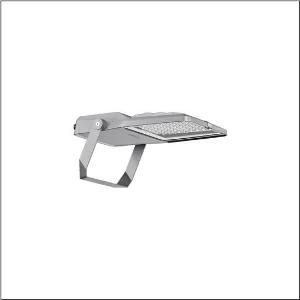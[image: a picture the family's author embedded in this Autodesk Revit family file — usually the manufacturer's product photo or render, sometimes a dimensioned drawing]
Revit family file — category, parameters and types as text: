
# Revit family: floodlight_fl_21_iq_mini___pl64_5xa7772d1e1a_af72
name_source: partatom
category: Lighting Fixtures
units: mm (PartAtom-declared; Revit-internal decimal feet)

## family parameters
Cut with Voids When Loaded = No
Host = Face
Light Source = No
Part Type = Normal
Room Calculation Point = No
Round Connector Dimension = Use Diameter
Shared = No

## types (1)
- --- (1 x LED, 14250 lm, 143 W, 2200K)
    Apparent Load = 143 VA
    CIE Flux Codes = 28 80 98 100 100
    Color Rendering = 70
    Color Temperature = 2200K
    Default Elevation = 1800 mm
    Description = Floodlight FL 21 iQ mini, floodlight, primary light control with lens, of PMMA, primary optical cover: protective disc, of toughened safety glass, transparent, light distribution: PL64, light emission: direct distribution, installation type: surface-mounted, LED, High Power LED, rated luminous flux: 14.250lm, luminous efficacy: 100lm/W, light colour: 722, colour temperature: 2200K, control: Street-Remote, Auto-Match, Temp-Guard, Night-Set, Smart-Wire, Desk-Remote (wireless, voltage-free reading and setting of iQ features in the workshop via application-optimized NFC function/RFID function), optimised constant luminous flux control (CLO 2.0), with terminal, 6-pole, mains connection: 220..240V, AC, 50/60Hz, start of lifetime: 143W, end of service life: 152W, reduction: 61W, luminaire housing, of diecast aluminium, powder-coated, Siteco® metallic grey (DB 702S), corrosivity category C5 mid according to DIN EN ISO 12944, sealing non-destructively replaceable, mounting bracket, of steel, galvanised, powder-coated, Siteco® metallic grey (DB 702S), protection rating (complete): IP66, insulation class (complete): insulation class II (safety insulation), certification: CE, ENEC, VDE, protection symbol: D, impact resistance: IK08, permissible operating ambient temperature: -40..+40°C, permissible operating ambient temperature for outdoor applications: -40..+50°C, standard: DIN EN 12944, LABS conformity tested according to VDMA 24364:2018-05, packaging unit: 1 piece

Light Distribution: PL64
    Height = 70 mm
    Lamp = 1 x LED
    Lamp Light Flux = 14250 lm
    Lamp Power = 143 W
    Lamp count = 1
    Length = 485 mm
    Luminous efficacy = 100 lm/W
    Manufacturer = Siteco
    ModVariant = No
    Model = 5XA7772D1E1A
    Number of Poles = 1
    OnlyDefault = Yes
    Power Factor = 1
    Product Name = Floodlight FL 21 iQ mini | PL64
    Product group = floodlight | pylon annexe
    ProductGroupID = 6200
    Protection Class = Protection class II
    Protection Degree = IP 66
    RLX_Detail_Level = 1
    RLX_Emergency_Light_Flux = 0 lm
    RLX_Emergency_Type = 0
    RLX_Emergency_Type_DB = No
    RlxData = <blob elided: 96453 chars, md5=e5577414>
    Socket = socket
    Standby Power = 0 W
    System Light Flux = 14250 lm
    System Power = 143 W
    Type Comments = factory setting: luminous flux: 100 % | dim-lin: 254 | 730 mA
    Type Image = l_1006845.jpg
    URL = http://relux.com
    VarID = @adj_098215
    Voltage = 0 V
    Weight = 0.00 kg
    Width = 337 mm

## geometry (parser evidence)
native form markers: Blend x4, Sweep x13
no freeform markers — native parametric forms only
